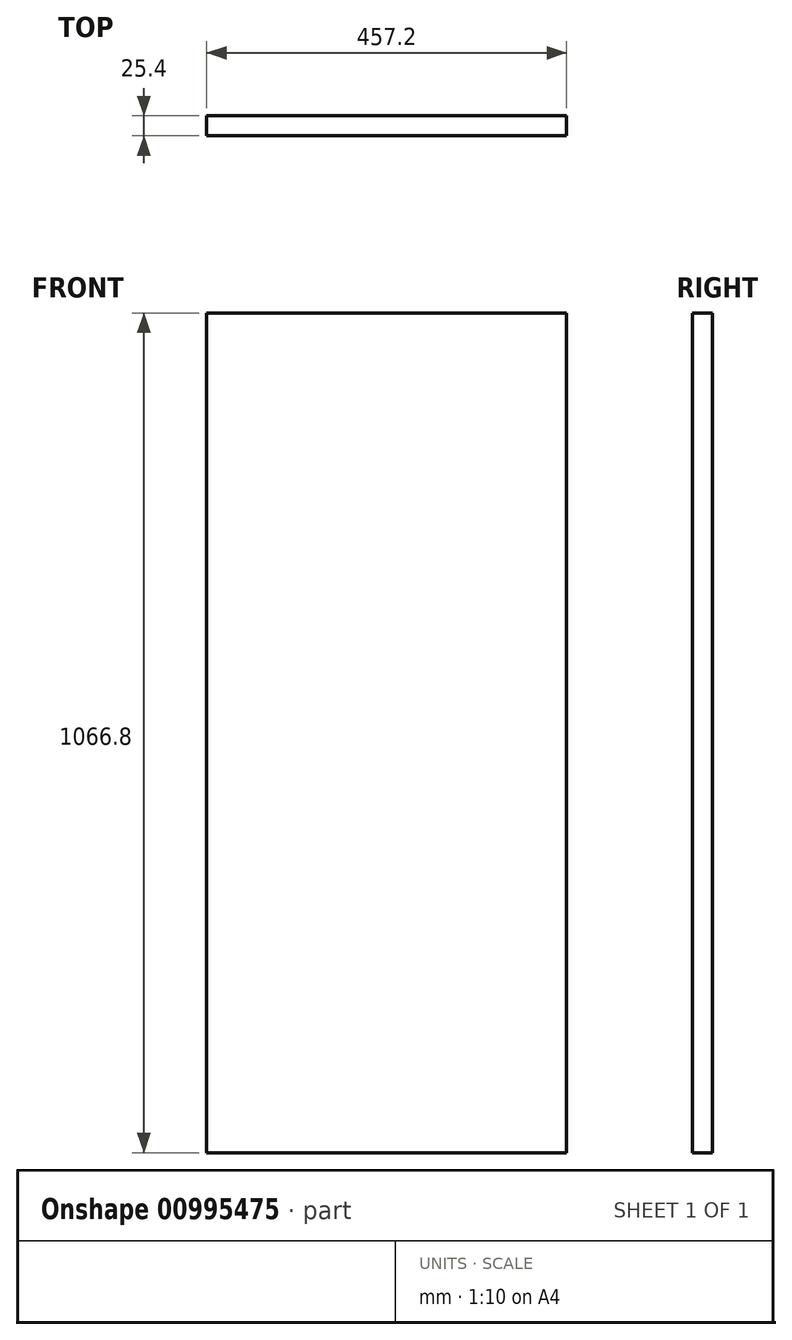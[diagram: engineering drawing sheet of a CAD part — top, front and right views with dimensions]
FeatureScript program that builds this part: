
annotation { "Feature Type Name" : "Feature", "Feature Type Description" : "" }
export const myFeature = defineFeature(function(context is Context, id is Id, definition is map)
    precondition{}
    {
        {
            var Q0;
            Q0=qCreatedBy(makeId("Front.planeOp"),FACE);
            var sketch = newSketch(context, id + "F0", { "sketchPlane" : qUnion([Q0])});
            skLineSegment(sketch, "E0.bottom", {"start": v(228.6, -533.4) * mm, "end": v(-228.6, -533.4) * mm});
            skLineSegment(sketch, "E0.top", {"start": v(228.6, 533.4) * mm, "end": v(-228.6, 533.4) * mm});
            skLineSegment(sketch, "E0.left", {"start": v(228.6, -533.4) * mm, "end": v(228.6, 533.4) * mm});
            skLineSegment(sketch, "E0.right", {"start": v(-228.6, -533.4) * mm, "end": v(-228.6, 533.4) * mm});
            skPoint(sketch, "E0.middle", {"position": v(0, 0) * mm});
            skSolve(sketch);
        }
        {
            var Q0;
            Q0 = qSketchRegion(id + "F0", true);
            extrude(context, id + "F1", {"entities" : qUnion([Q0]), "depth" : 25.4 * mm, "offsetDistance" : 25.4 * mm});
        }
    });
